# Revit family: Тактильная полиуретановая плитка диагональ(самоклеящеяся)
name_source: partatom
category: Оборудование
revit_build: Autodesk Revit 2017 (Build: 20160225_1515(x64)
units: mm (PartAtom-declared; Revit-internal decimal feet)

## family parameters
Общий = Да
Основа = Грань
При загрузке вырезать с полостями = Да
Размер круглого соединителя = Использовать диаметр
Тип детали = Нормальный
Точка расчета площади = Нет

## types (2) — shared parameters
ADSK_Наименование = Тактильная плитка полиуретан
ADSK_Размер_Высота рифа = 5 мм
ADSK_Размер_Габариты = 300Х300
ADSK_Размер_Длина = 300 мм
ADSK_Размер_Толщина = 2 мм
ADSK_Размер_Ширина = 300 мм
ADSK_Тип рифов = Рельефные полосы
URL = http://tiflocentre.ru
Изготовитель = ТИФЛОЦЕНТР «ВЕРТИКАЛЬ»
Применение = Улица/Помещение
Стоимость = 742 $
zero-valued in all types: Отметка по умолчанию

## per-type parameters (varying)
| type | ADSK_Код изделия | ADSK_Материал наименование | ADSK_Материал плитки | Описание |
| Тактильная плитка полиуретан (самоклеющаяся)_Желтая | 10131-1-ZH | Полиуретан, цвет желтый | Вертикаль_Полиуретан_Желтый | Тактильная ПУ плитка с рельефными диагоналями предназначена для информирования тлюдей с ограничениями зрения о смене направления пути. Желтый цвет плитки - отличный контраст по отношению к темному кафелю или асфальту, рекомендованный современными стандартами. Помимо высокой прочности и стойкости к погодным изменением, данная тактильная ПУ имеет клеящуюся основу, что упрощает монтаж в разы. Тактильная плитка ПУ от компании "Вертикаль"  протестирована незрячими специалистами  и одобрена ВОС. |
| Тактильная плитка полиуретановая (самоклеящаяся)_Черная | 10131-1-CH | Полиуретан, цвет черный | Вертикаль_Полиуретан_Черный | Тактильная плитка ПУ с диагоналями в виде рифоф предназначена для информирования людей с ограничениями зрения о смене направления движения на пути. Черный цвет плитки - важный контраст для слабовидящего цвета, который будет хорошо заметен на светлой поверхности. Отличительные особенности тактильной ПУ плитки от Тифлоцентра "Вертикаль" - всепогодность использования, износостойкость и самоклеящаяся основа, которая упрощает ее монтаж. Данная тактильная плитка протестирована незрячими специалистами и одобрена ВОС. |
